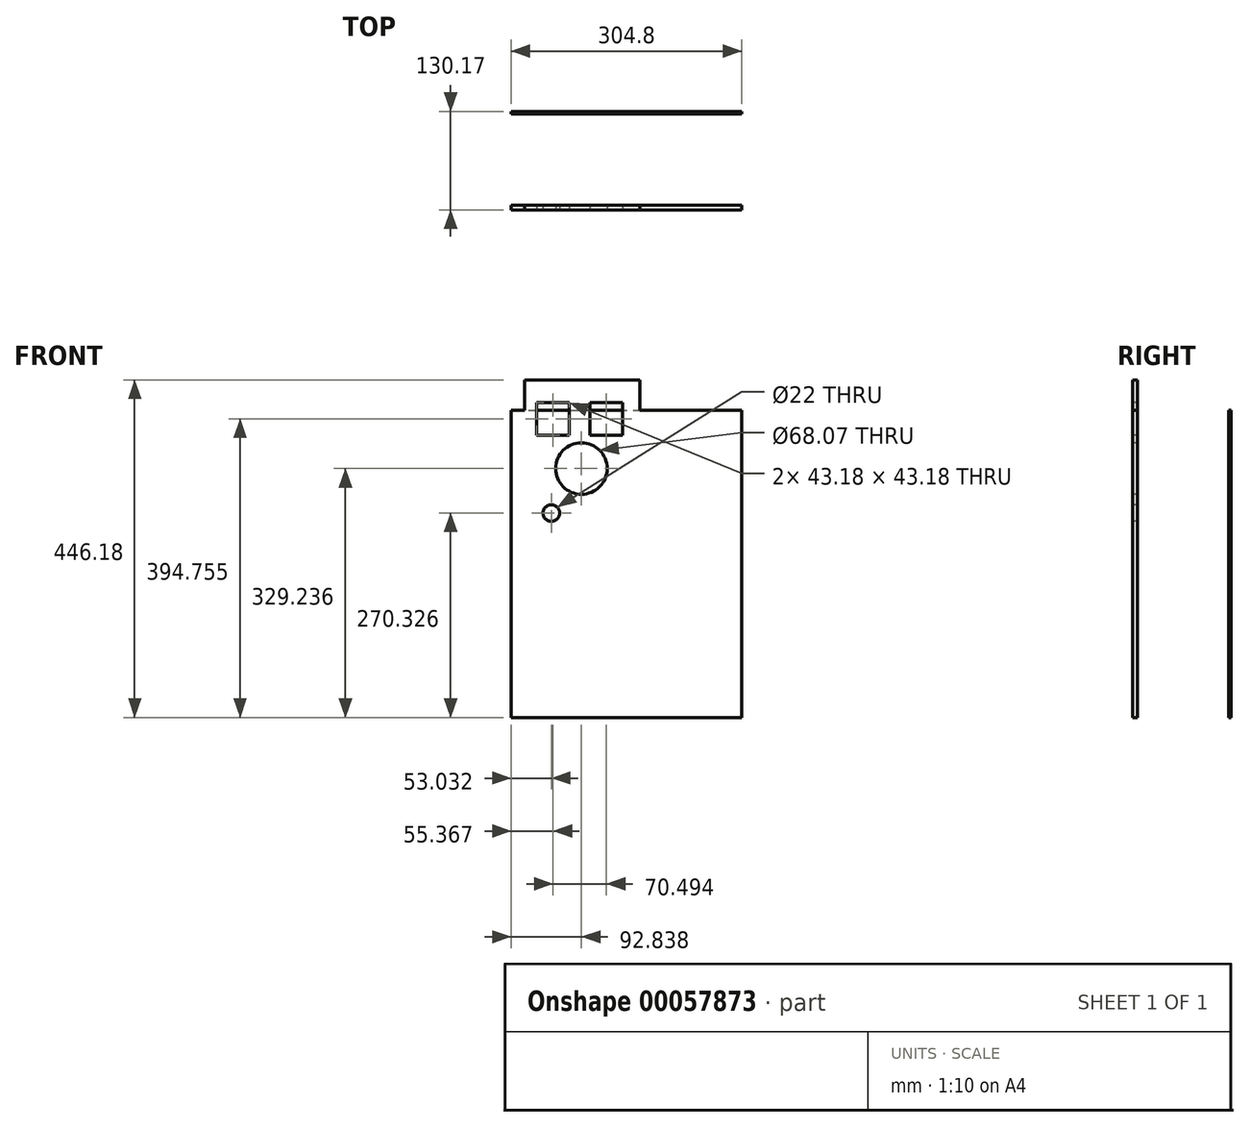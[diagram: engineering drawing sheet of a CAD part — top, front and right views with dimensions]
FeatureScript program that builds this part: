
annotation { "Feature Type Name" : "Feature", "Feature Type Description" : "" }
export const myFeature = defineFeature(function(context is Context, id is Id, definition is map)
    precondition{}
    {
        {
            var Q0;
            Q0=qCreatedBy(makeId("Front.planeOp"),FACE);
            var sketch = newSketch(context, id + "F0", { "sketchPlane" : qUnion([Q0])});
            skLineSegment(sketch, "E0.bottom", {"start": v(0, 0) * mm, "end": v(304.8, 0) * mm});
            skLineSegment(sketch, "E0.top", {"start": v(0, 406.4) * mm, "end": v(304.8, 406.4) * mm});
            skLineSegment(sketch, "E0.left", {"start": v(0, 0) * mm, "end": v(0, 406.4) * mm});
            skLineSegment(sketch, "E0.right", {"start": v(304.8, 0) * mm, "end": v(304.8, 406.4) * mm});
            skSolve(sketch);
        }
        {
            var Q0;
            Q0=makeQuery(id+"F0.imprint","IMPRINT",FACE,{"disambiguationData":[TD([[makeQuery(id+"F0.imprint","IMPRINT",EDGE,{"derivedFrom":sQuery(id+"F0.wireOp",EDGE,"E0.bottom")}),1.0]])]});
            extrude(context, id + "F1", {"entities" : qUnion([Q0]), "oppositeDirection" : true, "depth" : 3.17 * mm});
        }
        {
            var Q0;
            Q0=qCreatedBy(makeId("Front.planeOp"),FACE);
            cPlane(context, id + "F2", {"entities" : qUnion([Q0]), "cplaneType" : CPlaneType.OFFSET, "offset" : 127 * mm, "width" : 152.4 * mm, "height" : 152.4 * mm});
        }
        {
            var Q0;
            Q0=qCreatedBy(id+"F2.planeOp",FACE);
            var sketch = newSketch(context, id + "F3", { "sketchPlane" : qUnion([Q0])});
            skLineSegment(sketch, "E1.bottom", {"start": v(33.78, 416.35) * mm, "end": v(76.96, 416.35) * mm});
            skLineSegment(sketch, "E1.top", {"start": v(33.78, 373.17) * mm, "end": v(76.96, 373.17) * mm});
            skLineSegment(sketch, "E1.left", {"start": v(33.78, 416.35) * mm, "end": v(33.78, 373.17) * mm});
            skLineSegment(sketch, "E1.right", {"start": v(76.96, 416.35) * mm, "end": v(76.96, 373.17) * mm});
            skLineSegment(sketch, "E2.bottom", {"start": v(104.27, 416.35) * mm, "end": v(147.45, 416.35) * mm});
            skLineSegment(sketch, "E2.top", {"start": v(104.27, 373.17) * mm, "end": v(147.45, 373.17) * mm});
            skLineSegment(sketch, "E2.left", {"start": v(104.27, 416.35) * mm, "end": v(104.27, 373.17) * mm});
            skLineSegment(sketch, "E2.right", {"start": v(147.45, 416.35) * mm, "end": v(147.45, 373.17) * mm});
            skCircle(sketch, "E3", {"center": v(92.84, 329.24) * mm, "radius": 34.04 * mm});
            skLineSegment(sketch, "E4.0.0", {"start": v(0, 406.4) * mm, "end": v(0, 0) * mm});
            skLineSegment(sketch, "E4.0.1", {"start": v(0, 0) * mm, "end": v(304.8, 0) * mm});
            skLineSegment(sketch, "E4.0.2", {"start": v(304.8, 0) * mm, "end": v(304.8, 406.4) * mm});
            skLineSegment(sketch, "E4.0.3", {"start": v(304.8, 406.4) * mm, "end": v(0, 406.4) * mm});
            skLineSegment(sketch, "E5.bottom", {"start": v(17.46, 446.18) * mm, "end": v(169.86, 446.18) * mm});
            skLineSegment(sketch, "E5.top", {"start": v(17.46, 242.98) * mm, "end": v(169.86, 242.98) * mm});
            skLineSegment(sketch, "E5.left", {"start": v(17.46, 446.18) * mm, "end": v(17.46, 242.98) * mm});
            skLineSegment(sketch, "E5.right", {"start": v(169.86, 446.18) * mm, "end": v(169.86, 242.98) * mm});
            skCircle(sketch, "E6", {"center": v(53.03, 270.33) * mm, "radius": 11 * mm});
            skSolve(sketch);
        }
        {
            var Q0;
            Q0=makeQuery(id+"F1.opExtrude","SWEPT_FACE",FACE,{"disambiguationData":[OSD([sQuery(id+"F0.wireOp",EDGE,"E0.left")])]});
            cPlane(context, id + "F4", {"entities" : qUnion([Q0]), "cplaneType" : CPlaneType.OFFSET, "offset" : 0 * mm, "width" : 152.4 * mm, "height" : 152.4 * mm});
        }
        {
            var Q0;
            Q0 = qSketchRegion(id + "F3", true);
            extrude(context, id + "F5", {"entities" : qUnion([Q0]), "oppositeDirection" : true, "depth" : 6.35 * mm});
        }
    });
